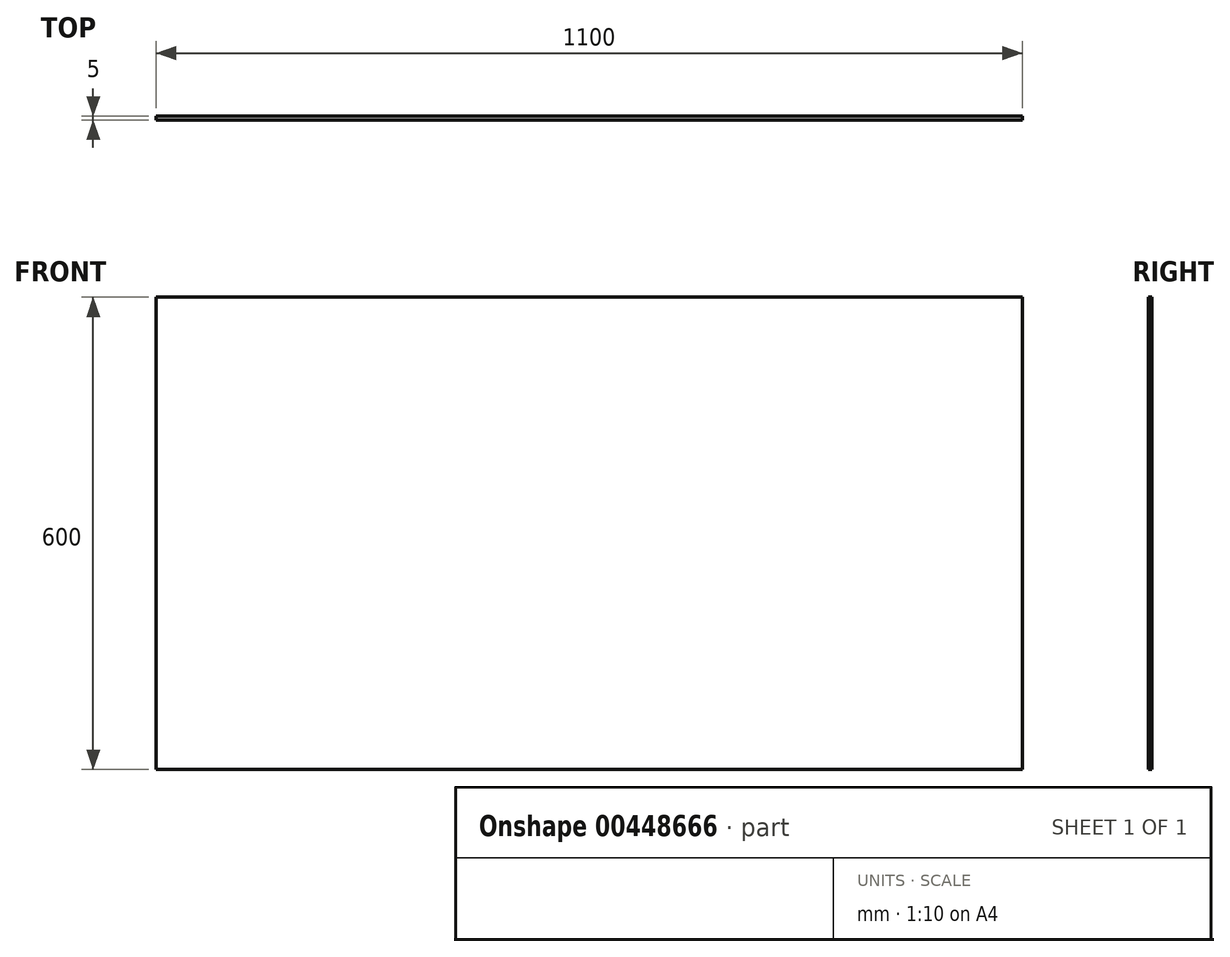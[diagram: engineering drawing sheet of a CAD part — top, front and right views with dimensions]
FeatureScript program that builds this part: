
annotation { "Feature Type Name" : "Feature", "Feature Type Description" : "" }
export const myFeature = defineFeature(function(context is Context, id is Id, definition is map)
    precondition{}
    {
        {
            var Q0;
            Q0=qCreatedBy(makeId("Front.planeOp"),FACE);
            var sketch = newSketch(context, id + "F0", { "sketchPlane" : qUnion([Q0])});
            skLineSegment(sketch, "E0.bottom", {"start": v(550, -300) * mm, "end": v(-550, -300) * mm});
            skLineSegment(sketch, "E0.top", {"start": v(550, 300) * mm, "end": v(-550, 300) * mm});
            skLineSegment(sketch, "E0.left", {"start": v(550, -300) * mm, "end": v(550, 300) * mm});
            skLineSegment(sketch, "E0.right", {"start": v(-550, -300) * mm, "end": v(-550, 300) * mm});
            skPoint(sketch, "E0.middle", {"position": v(0, 0) * mm});
            skSolve(sketch);
        }
        {
            var Q0;
            Q0 = qSketchRegion(id + "F0", true);
            extrude(context, id + "F1", {"entities" : qUnion([Q0]), "depth" : 5 * mm, "offsetDistance" : 25 * mm});
        }
    });
